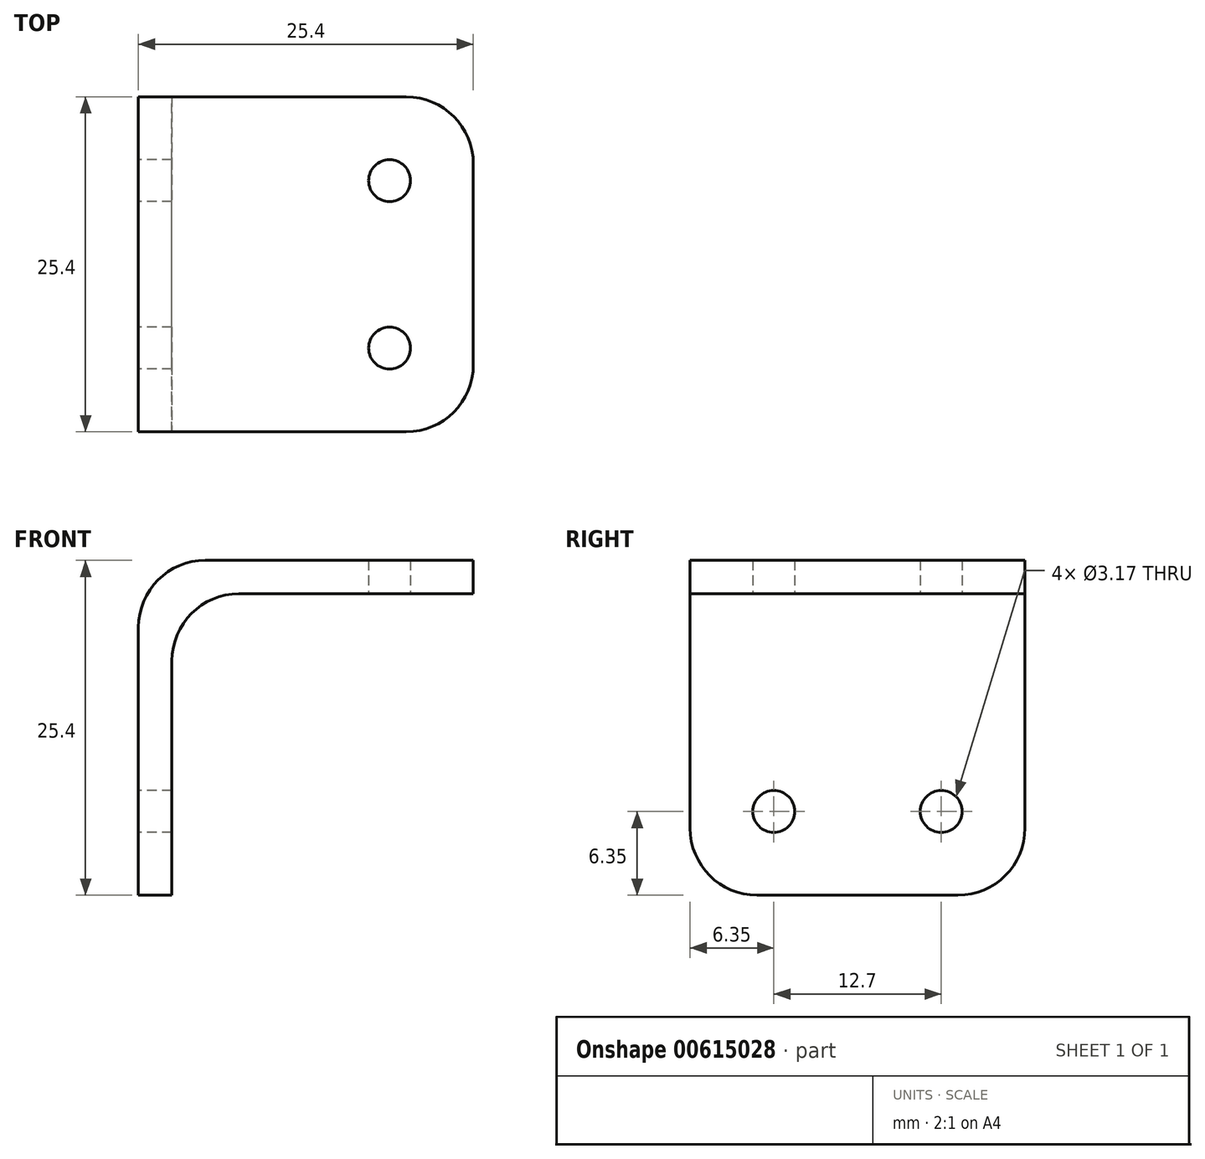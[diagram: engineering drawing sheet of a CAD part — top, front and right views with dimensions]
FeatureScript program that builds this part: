
annotation { "Feature Type Name" : "Feature", "Feature Type Description" : "" }
export const myFeature = defineFeature(function(context is Context, id is Id, definition is map)
    precondition{}
    {
        {
            var Q0;
            Q0=qCreatedBy(makeId("Front.planeOp"),FACE);
            var sketch = newSketch(context, id + "F0", { "sketchPlane" : qUnion([Q0])});
            skLineSegment(sketch, "E0", {"start": v(0, 0) * mm, "end": v(0, 25.4) * mm});
            skLineSegment(sketch, "E1", {"start": v(0, 25.4) * mm, "end": v(25.4, 25.4) * mm});
            skLineSegment(sketch, "E2.0", {"start": v(2.54, 22.86) * mm, "end": v(25.4, 22.86) * mm});
            skLineSegment(sketch, "E2.1", {"start": v(2.54, 0) * mm, "end": v(2.54, 22.86) * mm});
            skLineSegment(sketch, "E3", {"start": v(0, 0) * mm, "end": v(2.54, 0) * mm});
            skLineSegment(sketch, "E4", {"start": v(25.4, 22.86) * mm, "end": v(25.4, 25.4) * mm});
            skSolve(sketch);
        }
        {
            var Q0;
            Q0=qCreatedBy(makeId("Top.planeOp"),FACE);
            var sketch = newSketch(context, id + "F1", { "sketchPlane" : qUnion([Q0])});
            skLineSegment(sketch, "E5", {"start": v(25.4, 0) * mm, "end": v(25.4, -12.7) * mm});
            skLineSegment(sketch, "E6", {"start": v(25.4, -12.7) * mm, "end": v(2.54, -12.7) * mm});
            skLineSegment(sketch, "E7", {"start": v(2.54, -12.7) * mm, "end": v(2.54, 0) * mm});
            skLineSegment(sketch, "E8.MirrorCS", {"start": v(25.4, 12.7) * mm, "end": v(2.54, 12.7) * mm});
            skLineSegment(sketch, "E9.MirrorCS", {"start": v(2.54, 12.7) * mm, "end": v(2.54, 0) * mm});
            skLineSegment(sketch, "E10.MirrorCS", {"start": v(25.4, 0) * mm, "end": v(25.4, 12.7) * mm});
            skLineSegment(sketch, "E11", {"start": v(25.4, 0) * mm, "end": v(19.05, 0) * mm});
            skLineSegment(sketch, "E12.0", {"start": v(25.4, 6.35) * mm, "end": v(19.05, 6.35) * mm});
            skLineSegment(sketch, "E13.0", {"start": v(25.4, -6.35) * mm, "end": v(19.05, -6.35) * mm});
            skCircle(sketch, "E14", {"center": v(19.05, -6.35) * mm, "radius": 1.59 * mm});
            skCircle(sketch, "E15", {"center": v(19.05, 6.35) * mm, "radius": 1.59 * mm});
            skSolve(sketch);
        }
        {
            var Q0;
            Q0=qCreatedBy(makeId("Right.planeOp"),FACE);
            var sketch = newSketch(context, id + "F2", { "sketchPlane" : qUnion([Q0])});
            skLineSegment(sketch, "E16", {"start": v(0, 0) * mm, "end": v(-12.7, 0) * mm});
            skLineSegment(sketch, "E17", {"start": v(-12.7, 0) * mm, "end": v(-12.7, 25.4) * mm});
            skLineSegment(sketch, "E18", {"start": v(-12.7, 25.4) * mm, "end": v(0, 25.4) * mm});
            skLineSegment(sketch, "E19.MirrorCS", {"start": v(12.7, 25.4) * mm, "end": v(0, 25.4) * mm});
            skLineSegment(sketch, "E20.MirrorCS", {"start": v(12.7, 0) * mm, "end": v(12.7, 25.4) * mm});
            skLineSegment(sketch, "E21.MirrorCS", {"start": v(0, 0) * mm, "end": v(12.7, 0) * mm});
            skLineSegment(sketch, "E22.0", {"start": v(6.35, 0) * mm, "end": v(6.35, 6.35) * mm});
            skLineSegment(sketch, "E23.0", {"start": v(-6.35, 0) * mm, "end": v(-6.35, 6.35) * mm});
            skPoint(sketch, "E24.orphan", {"position": v(0, 22.86) * mm});
            skCircle(sketch, "E25", {"center": v(-6.35, 6.35) * mm, "radius": 1.59 * mm});
            skCircle(sketch, "E26", {"center": v(6.35, 6.35) * mm, "radius": 1.59 * mm});
            skSolve(sketch);
        }
        {
            var Q0;
            Q0=makeQuery(id+"F0.imprint","IMPRINT",FACE,{"disambiguationData":[TD([[makeQuery(id+"F0.imprint","IMPRINT",EDGE,{"derivedFrom":sQuery(id+"F0.wireOp",EDGE,"E0")}),-1.0]])]});
            extrude(context, id + "F3", {"entities" : qUnion([Q0]), "endBound" : BoundingType.SYMMETRIC, "depth" : 25.4 * mm, "offsetDistance" : 25.4 * mm});
        }
        {
            var Q0;
            Q0=makeQuery(id+"F1.imprint","IMPRINT",FACE,{"disambiguationData":[TD([[makeQuery(id+"F1.imprint","IMPRINT",EDGE,{"derivedFrom":sQuery(id+"F1.wireOp",EDGE,"E15")}),1.0]])]});
            var Q1;
            Q1=makeQuery(id+"F1.imprint","IMPRINT",FACE,{"disambiguationData":[TD([[makeQuery(id+"F1.imprint","IMPRINT",EDGE,{"derivedFrom":sQuery(id+"F1.wireOp",EDGE,"E14")}),1.0]])]});
            extrude(context, id + "F4", {"entities" : qUnion([Q0, Q1]), "operationType" : NewBodyOperationType.REMOVE, "depth" : 39.37 * mm, "offsetDistance" : 25.4 * mm});
        }
        {
            var Q0;
            Q0=makeQuery(id+"F2.imprint","IMPRINT",FACE,{"disambiguationData":[TD([[makeQuery(id+"F2.imprint","IMPRINT",EDGE,{"derivedFrom":sQuery(id+"F2.wireOp",EDGE,"E26")}),1.0]])]});
            var Q1;
            Q1=makeQuery(id+"F2.imprint","IMPRINT",FACE,{"disambiguationData":[TD([[makeQuery(id+"F2.imprint","IMPRINT",EDGE,{"derivedFrom":sQuery(id+"F2.wireOp",EDGE,"E25")}),1.0]])]});
            extrude(context, id + "F5", {"entities" : qUnion([Q0, Q1]), "operationType" : NewBodyOperationType.REMOVE, "depth" : 8.38 * mm, "offsetDistance" : 25.4 * mm});
        }
        {
            var Q0;
            Q0=makeQuery(id+"F3.opExtrude","CAP_EDGE",EDGE,{"disambiguationData":[OSD([sQuery(id+"F0.wireOp",EDGE,"E4")])],"isStart":false});
            var Q1;
            Q1=makeQuery(id+"F3.opExtrude","CAP_EDGE",EDGE,{"disambiguationData":[OSD([sQuery(id+"F0.wireOp",EDGE,"E4")])],"isStart":true});
            var Q2;
            Q2=makeQuery(id+"F3.opExtrude","CAP_EDGE",EDGE,{"disambiguationData":[OSD([sQuery(id+"F0.wireOp",EDGE,"E3")])],"isStart":false});
            var Q3;
            Q3=makeQuery(id+"F3.opExtrude","CAP_EDGE",EDGE,{"disambiguationData":[OSD([sQuery(id+"F0.wireOp",EDGE,"E3")])],"isStart":true});
            fillet(context, id + "F6", {"entities" : qUnion([Q0, Q1, Q2, Q3]), "radius" : 5.08 * mm, "tangentPropagation" : true, "allowEdgeOverflow" : false});
        }
        {
            var Q0;
            Q0=makeQuery(id+"F3.opExtrude","SWEPT_EDGE",EDGE,{"disambiguationData":[OSD([sQuery(id+"F0.wireOp",EDGE,"E0"),sQuery(id+"F0.wireOp",EDGE,"E1")])]});
            fillet(context, id + "F7", {"entities" : qUnion([Q0]), "radius" : 5.08 * mm, "tangentPropagation" : true, "allowEdgeOverflow" : false});
        }
        {
            var Q0;
            Q0=makeQuery(id+"F3.opExtrude","SWEPT_EDGE",EDGE,{"disambiguationData":[OSD([sQuery(id+"F0.wireOp",EDGE,"E2.0"),sQuery(id+"F0.wireOp",EDGE,"E2.1")])]});
            fillet(context, id + "F8", {"entities" : qUnion([Q0]), "radius" : 5.08 * mm, "tangentPropagation" : true, "allowEdgeOverflow" : false});
        }
    });
